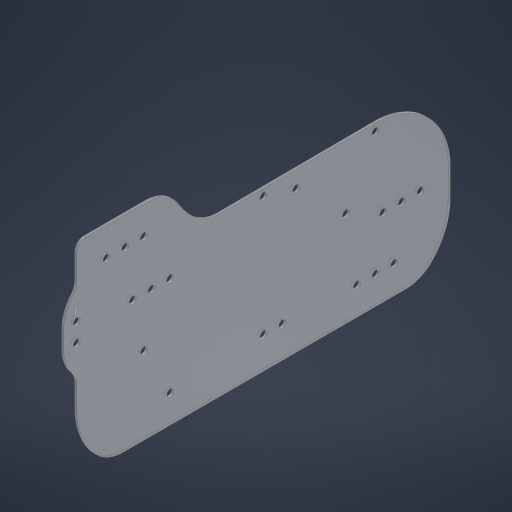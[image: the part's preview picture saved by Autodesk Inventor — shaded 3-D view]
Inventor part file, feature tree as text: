
AUTODESK INVENTOR PART (.ipt)
format: ipt  version: 2024 (Build 280153000, 153)  size: 343,040 bytes
history: native  units: in
note: dims shown in document units (in); Inventor stores cm internally (conversion verified against a paired STEP export)
features: sketch x1, extrude x1, hole x1
ambient origin geometry x8: Origin, YZ Plane, XZ Plane, XY Plane, X Axis, Y Axis, Z Axis, Center Point
bodies: Solid1 (feature_tree)
feature tree (3):
  sketch  "Sketch1"  dims[d4=0.0625in d5=0.0in d81=1.325in d82=1.5in d83=1.325in d84=1.5in d85=1.5in d88=0.5in d89=0.5in d90=0.5in d91=0.5in d92=1.0in d93=1.0in d94=1.5in d95=1.5in d96=0.5in d97=0.5in d98=1.325in d99=1.5in d100=0.5in d101=0.5in d102=0.1875in d103=0.75in d104=0.375in d105=0.25in d106=0.5635in d107=1.0in d108=0.8108in d109=1.5in d110=1.5in d111=0.25in d112=0.25in d122=0.75in d123=2.5in d124=7.5in d125=4.0in d126=1.5in d127=4.0in d128=1.5in d129=1.5in d130=0.875in d131=0.875in d132=1.723in d133=1.972in d134=1.0in d135=1.25in d136=2.875in d137=3.934in d138=1.0in d139=2.46in d140=1.0in d141=0.25in d142=0.35in d143=0.35in d144=0.5in d145=0.75in d146=0.75in d147=1.0in d148=1.0in d149=0.5in d150=1.0in d151=0.25in d152=1.5in d153=0.0625in d154=3.0in d155=1.0in d159=0.1in d160=0.2in d161=0.875in d162=1.51in d163=0.793in]
  extrude  "Extrusion1"  Depth=1.0in
  hole  "Hole4"  [1 undecoded]
note: 1 required parameter value undecoded (feature->parameter linkage not recoverable at this tier; creation-order binding heuristic only, values carry confidence <= 0.55)
